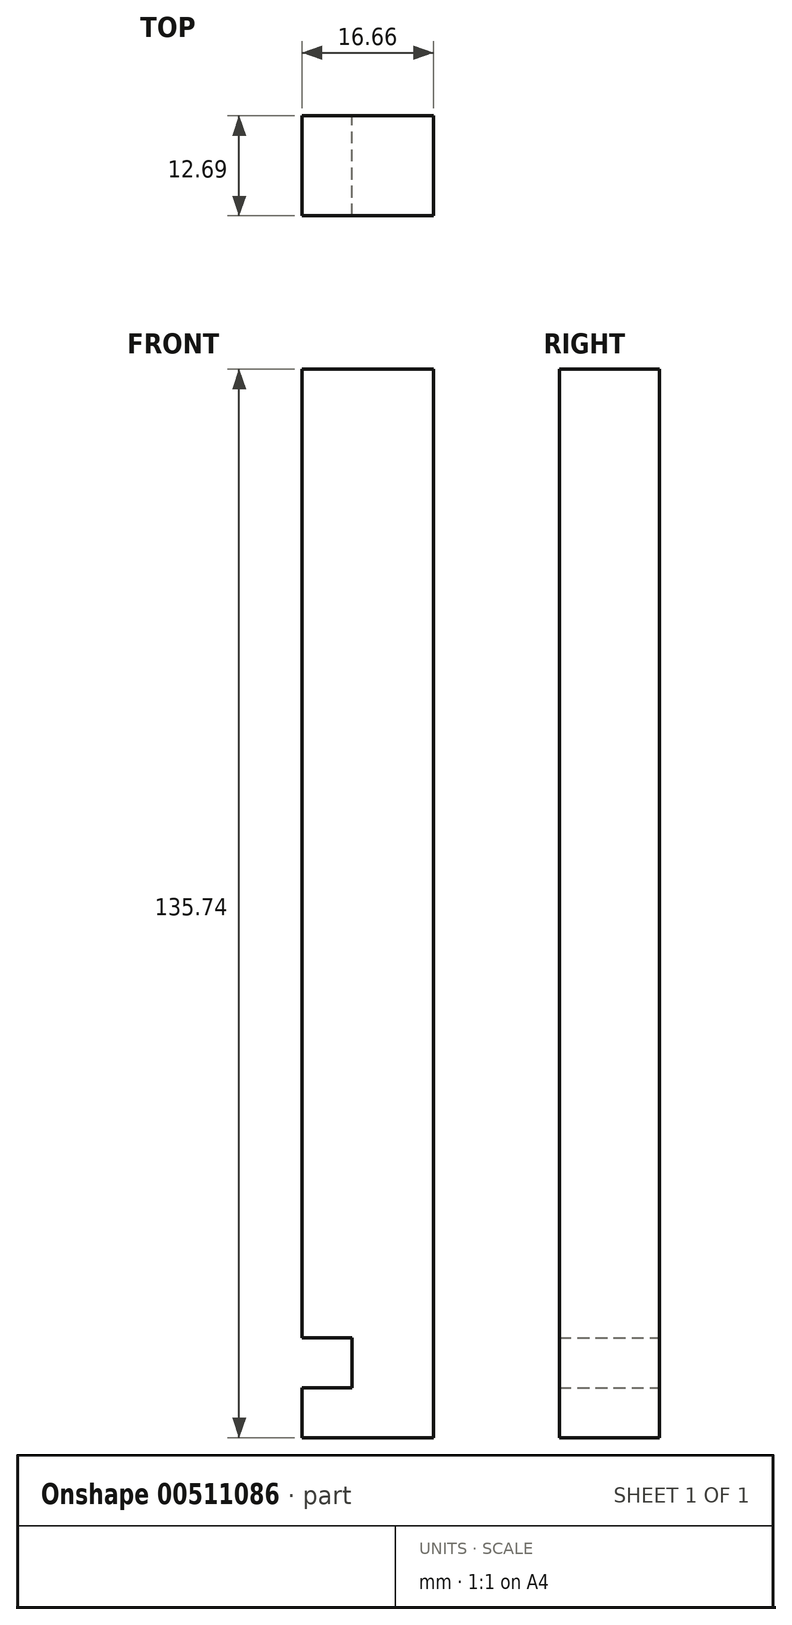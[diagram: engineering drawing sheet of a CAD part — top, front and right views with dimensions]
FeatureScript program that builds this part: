
annotation { "Feature Type Name" : "Feature", "Feature Type Description" : "" }
export const myFeature = defineFeature(function(context is Context, id is Id, definition is map)
    precondition{}
    {
        {
            assignVariable(context, id + "F0", {"name" : "thickness", "anyValue" : 0.66});
        }
        {
            assignVariable(context, id + "F1", {"name" : "bodyLength", "anyValue" : 14});
        }
        {
            var Q0;
            Q0=qCreatedBy(makeId("Front.planeOp"),FACE);
            var sketch = newSketch(context, id + "F2", { "sketchPlane" : qUnion([Q0])});
            skLineSegment(sketch, "E0", {"start": v(-6.35, 123.04) * mm, "end": v(-6.35, 0) * mm});
            skLineSegment(sketch, "E1", {"start": v(-6.35, 0) * mm, "end": v(0, 0) * mm});
            skLineSegment(sketch, "E2", {"start": v(0, 0) * mm, "end": v(0, -6.35) * mm});
            skLineSegment(sketch, "E3", {"start": v(0, -6.35) * mm, "end": v(-6.35, -6.35) * mm});
            skLineSegment(sketch, "E4", {"start": v(-6.35, -6.35) * mm, "end": v(-6.35, -12.7) * mm});
            skLineSegment(sketch, "E5", {"start": v(-6.35, -12.7) * mm, "end": v(10.31, -12.7) * mm});
            skLineSegment(sketch, "E6", {"start": v(10.31, -12.7) * mm, "end": v(10.31, 123.04) * mm});
            skLineSegment(sketch, "E7", {"start": v(10.31, 123.04) * mm, "end": v(-6.35, 123.04) * mm});
            skSolve(sketch);
        }
        {
            var Q0;
            Q0=makeQuery(id+"F2.imprint","IMPRINT",FACE,{"disambiguationData":[TD([[makeQuery(id+"F2.imprint","IMPRINT",EDGE,{"derivedFrom":sQuery(id+"F2.wireOp",EDGE,"E0")}),1.0]])]});
            extrude(context, id + "F3", {"entities" : qUnion([Q0]), "depth" : (getVariable(context, 'bodyLength') - (getVariable(context, 'thickness') * 2)) * mm, "offsetDistance" : 25.4 * mm});
        }
    });
